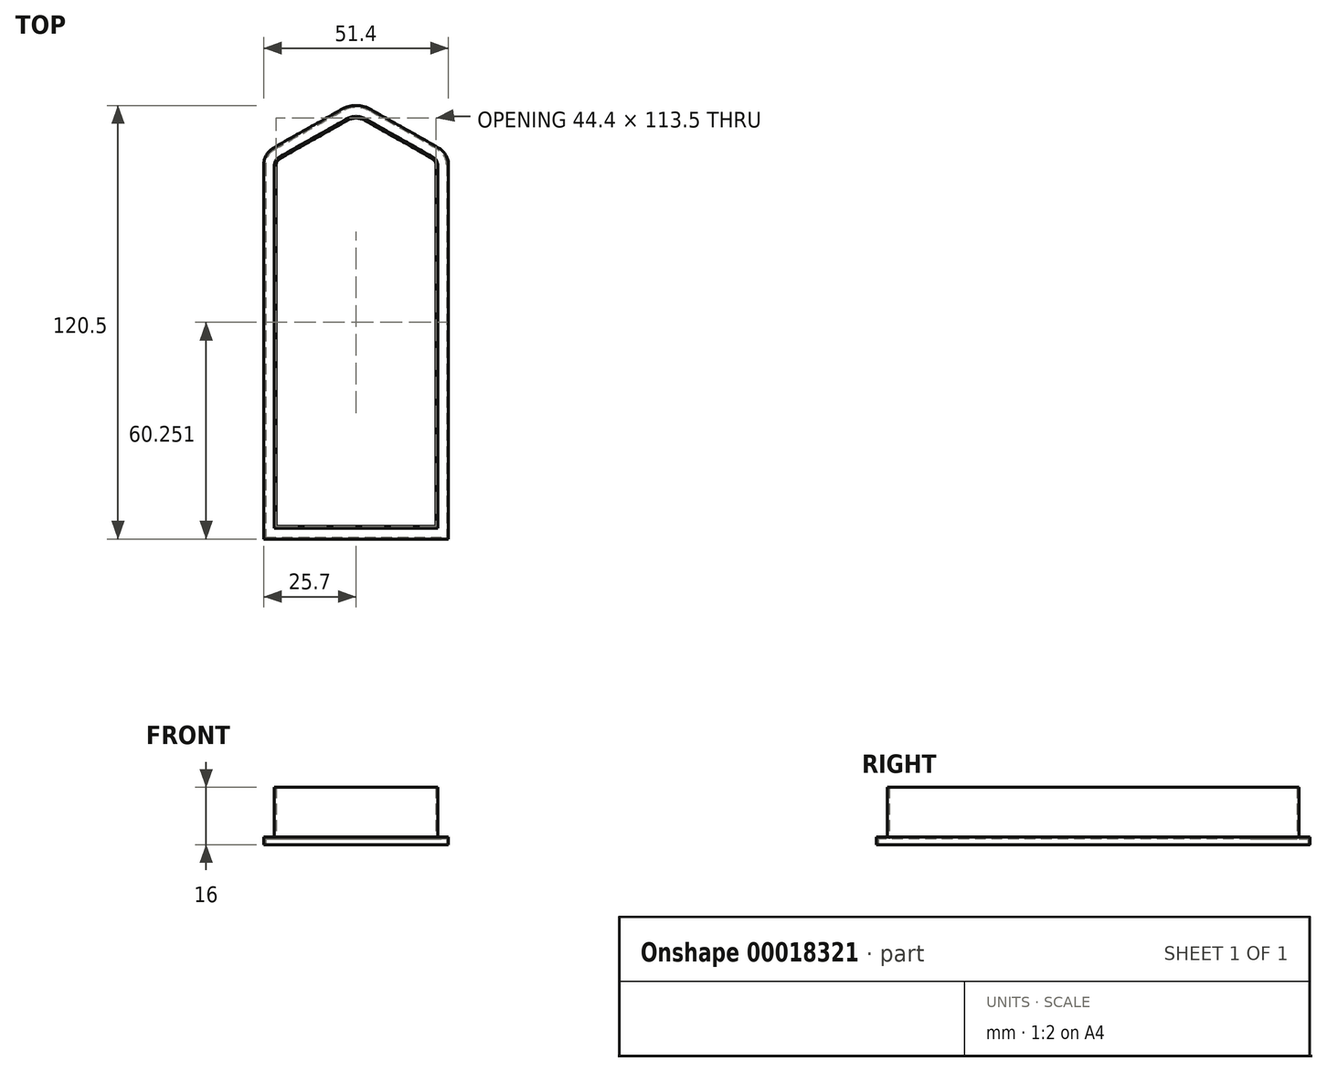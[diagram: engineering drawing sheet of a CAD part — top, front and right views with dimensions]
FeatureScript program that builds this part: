
annotation { "Feature Type Name" : "Feature", "Feature Type Description" : "" }
export const myFeature = defineFeature(function(context is Context, id is Id, definition is map)
    precondition{}
    {
        {
            var Q0;
            Q0=qCreatedBy(makeId("Top.planeOp"),FACE);
            var sketch = newSketch(context, id + "F0", { "sketchPlane" : qUnion([Q0])});
            skLineSegment(sketch, "E0", {"start": v(22.2, 27.41) * mm, "end": v(22.2, -73.05) * mm});
            skLineSegment(sketch, "E1", {"start": v(22.2, -73.05) * mm, "end": v(0, -73.05) * mm});
            skFitSpline(sketch, "E2", {"points": [v(22.2, 28.55) * mm, v(0, 41.25) * mm], "startDerivative": vector(-22.2, 13.23) * mm, "endDerivative": vector(-22.2, 13.23) * mm});
            skFitSpline(sketch, "E3.MirrorCS", {"points": [v(-22.2, 28.55) * mm, v(0, 41.25) * mm], "startDerivative": vector(22.2, 13.23) * mm, "endDerivative": vector(22.2, 13.23) * mm});
            skLineSegment(sketch, "E4.MirrorCS", {"start": v(-22.2, 27.41) * mm, "end": v(-22.2, -73.05) * mm});
            skLineSegment(sketch, "E5.MirrorCS", {"start": v(-22.2, -73.05) * mm, "end": v(0, -73.05) * mm});
            skArc(sketch, "E6.filletArc", {"start": v(2.51, 39.77) * mm, "mid": v(0, 40.45) * mm, "end": v(-2.51, 39.77) * mm});
            skArc(sketch, "E7.filletArc", {"start": v(-21.22, 29.14) * mm, "mid": v(-21.94, 28.4) * mm, "end": v(-22.2, 27.41) * mm});
            skArc(sketch, "E8.filletArc", {"start": v(22.2, 27.41) * mm, "mid": v(21.94, 28.4) * mm, "end": v(21.22, 29.14) * mm});
            skSolve(sketch);
        }
        {
            var Q0;
            Q0=makeQuery(id+"F0.imprint","IMPRINT",FACE,{"disambiguationData":[TD([[makeQuery(id+"F0.imprint","IMPRINT",EDGE,{"derivedFrom":sQuery(id+"F0.wireOp",EDGE,"E0")}),-1.0]])]});
            extrude(context, id + "F1", {"entities" : qUnion([Q0]), "depth" : 1.7 * mm});
        }
        {
            var Q0;
            Q0=makeQuery(id+"F1.opExtrude","SWEPT_BODY",BODY,{"disambiguationData":[OSD([sQuery(id+"F0.wireOp",EDGE,"E0"),sQuery(id+"F0.wireOp",EDGE,"E1"),sQuery(id+"F0.wireOp",EDGE,"E2"),sQuery(id+"F0.wireOp",EDGE,"E3.MirrorCS"),sQuery(id+"F0.wireOp",EDGE,"E4.MirrorCS"),sQuery(id+"F0.wireOp",EDGE,"E5.MirrorCS")])]});
            transform(context, id + "F2", {"entities" : qUnion([Q0]), "transformType" : TransformType.TRANSLATION_3D, "dx" : 0 * mm, "dy" : 0 * mm, "dz" : 0 * mm, "makeCopy" : true});
        }
        {
            var Q0;
            Q0=makeQuery(id+"F1.opExtrude","CAP_FACE",FACE,{"disambiguationData":[OSD([sQuery(id+"F0.wireOp",EDGE,"E0"),sQuery(id+"F0.wireOp",EDGE,"E1"),sQuery(id+"F0.wireOp",EDGE,"E2"),sQuery(id+"F0.wireOp",EDGE,"E3.MirrorCS"),sQuery(id+"F0.wireOp",EDGE,"E4.MirrorCS"),sQuery(id+"F0.wireOp",EDGE,"E5.MirrorCS")])],"isStart":false});
            var Q1;
            Q1=makeQuery(id+"F1.opExtrude","CAP_FACE",FACE,{"disambiguationData":[OSD([sQuery(id+"F0.wireOp",EDGE,"E0"),sQuery(id+"F0.wireOp",EDGE,"E1"),sQuery(id+"F0.wireOp",EDGE,"E2"),sQuery(id+"F0.wireOp",EDGE,"E3.MirrorCS"),sQuery(id+"F0.wireOp",EDGE,"E4.MirrorCS"),sQuery(id+"F0.wireOp",EDGE,"E5.MirrorCS")])],"isStart":true});
            shell(context, id + "F3", {"entities" : qUnion([Q0, Q1]), "thickness" : 3 * mm, "oppositeDirection" : true});
        }
        {
            var Q0;
            Q0=makeQuery(id+"F2.opPattern","COPY",FACE,{"derivedFrom":makeQuery(id+"F1.opExtrude","CAP_FACE",FACE,{"disambiguationData":[OSD([sQuery(id+"F0.wireOp",EDGE,"E0"),sQuery(id+"F0.wireOp",EDGE,"E1"),sQuery(id+"F0.wireOp",EDGE,"E2"),sQuery(id+"F0.wireOp",EDGE,"E3.MirrorCS"),sQuery(id+"F0.wireOp",EDGE,"E4.MirrorCS"),sQuery(id+"F0.wireOp",EDGE,"E5.MirrorCS")])],"isStart":false}),"instanceName":"1"});
            extrude(context, id + "F4", {"entities" : qUnion([Q0]), "operationType" : NewBodyOperationType.ADD, "depth" : 14.3 * mm});
        }
        {
            var Q0;
            Q0=makeQuery(id+"F4.opExtrude","CAP_FACE",FACE,{"disambiguationData":[OSD([sQuery(id+"F0.wireOp",EDGE,"E0"),sQuery(id+"F0.wireOp",EDGE,"E1"),sQuery(id+"F0.wireOp",EDGE,"E2"),sQuery(id+"F0.wireOp",EDGE,"E3.MirrorCS"),sQuery(id+"F0.wireOp",EDGE,"E4.MirrorCS"),sQuery(id+"F0.wireOp",EDGE,"E5.MirrorCS")])],"isStart":false});
            var Q1;
            Q1=makeQuery(id+"F2.opPattern","COPY",FACE,{"derivedFrom":makeQuery(id+"F1.opExtrude","CAP_FACE",FACE,{"disambiguationData":[OSD([sQuery(id+"F0.wireOp",EDGE,"E0"),sQuery(id+"F0.wireOp",EDGE,"E1"),sQuery(id+"F0.wireOp",EDGE,"E2"),sQuery(id+"F0.wireOp",EDGE,"E3.MirrorCS"),sQuery(id+"F0.wireOp",EDGE,"E4.MirrorCS"),sQuery(id+"F0.wireOp",EDGE,"E5.MirrorCS")])],"isStart":true}),"instanceName":"1"});
            shell(context, id + "F5", {"entities" : qUnion([Q0, Q1]), "thickness" : .5 * mm, "oppositeDirection" : true});
        }
    });
